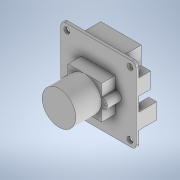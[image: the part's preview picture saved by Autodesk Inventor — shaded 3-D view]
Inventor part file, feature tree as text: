
AUTODESK INVENTOR PART (.ipt)
format: ipt  version: 2020 (Build 240168000, 168)  size: 314,368 bytes
history: native  units: mm
features: sketch x12, extrude x11, other x3, fillet x2, projected_geometry x2, chamfer x1, revolve x1
ambient origin geometry x8: Origin, YZ Plane, XZ Plane, XY Plane, X Axis, Y Axis, Z Axis, Center Point
bodies: Body1 (feature_tree)
feature tree (32):
  other  "Trackingcam (Applied robotics)"
  other  "Твердое тело1"
  extrude  "Выдавливание1"  Depth=38.0mm
  fillet  "Сопряжение1"  Radius=38.0mm
  extrude  "Выдавливание2"  Depth=3.0mm
  extrude  "Выдавливание3"  Depth=3.0mm
  extrude  "Выдавливание4"  Depth=3.0mm
  extrude  "Выдавливание5"  Depth=20.0mm
  chamfer  "Фаска1"  Distance=1.4mm
  extrude  "Выдавливание6"  Depth=2.0mm
  extrude  "Выдавливание7"  Depth=8.5mm
  extrude  "Выдавливание8"  Depth=10.5mm
  extrude  "Выдавливание9"  Depth=17.0mm
  extrude  "Выдавливание10"  Depth=17.0mm
  extrude  "Выдавливание11"  Depth=7.0mm TaperAngle=0.0deg
  fillet  "Сопряжение2"  Radius=13.0mm
  other  "РабПлоскость1"
  revolve  "Вращение1"
  sketch  "Эскиз1"
  sketch  "Эскиз2"
  sketch  "Эскиз3"
  sketch  "Эскиз4"
  sketch  "Эскиз5"
  sketch  "Эскиз6"
  sketch  "Эскиз7"
  sketch  "Эскиз8"
  sketch  "Эскиз9"
  sketch  "Эскиз11"
  projected_geometry  "Спроецированная петля1"
  projected_geometry  "Спроецированная петля2"
  sketch  "Эскиз12"
  sketch  "Эскиз13"
